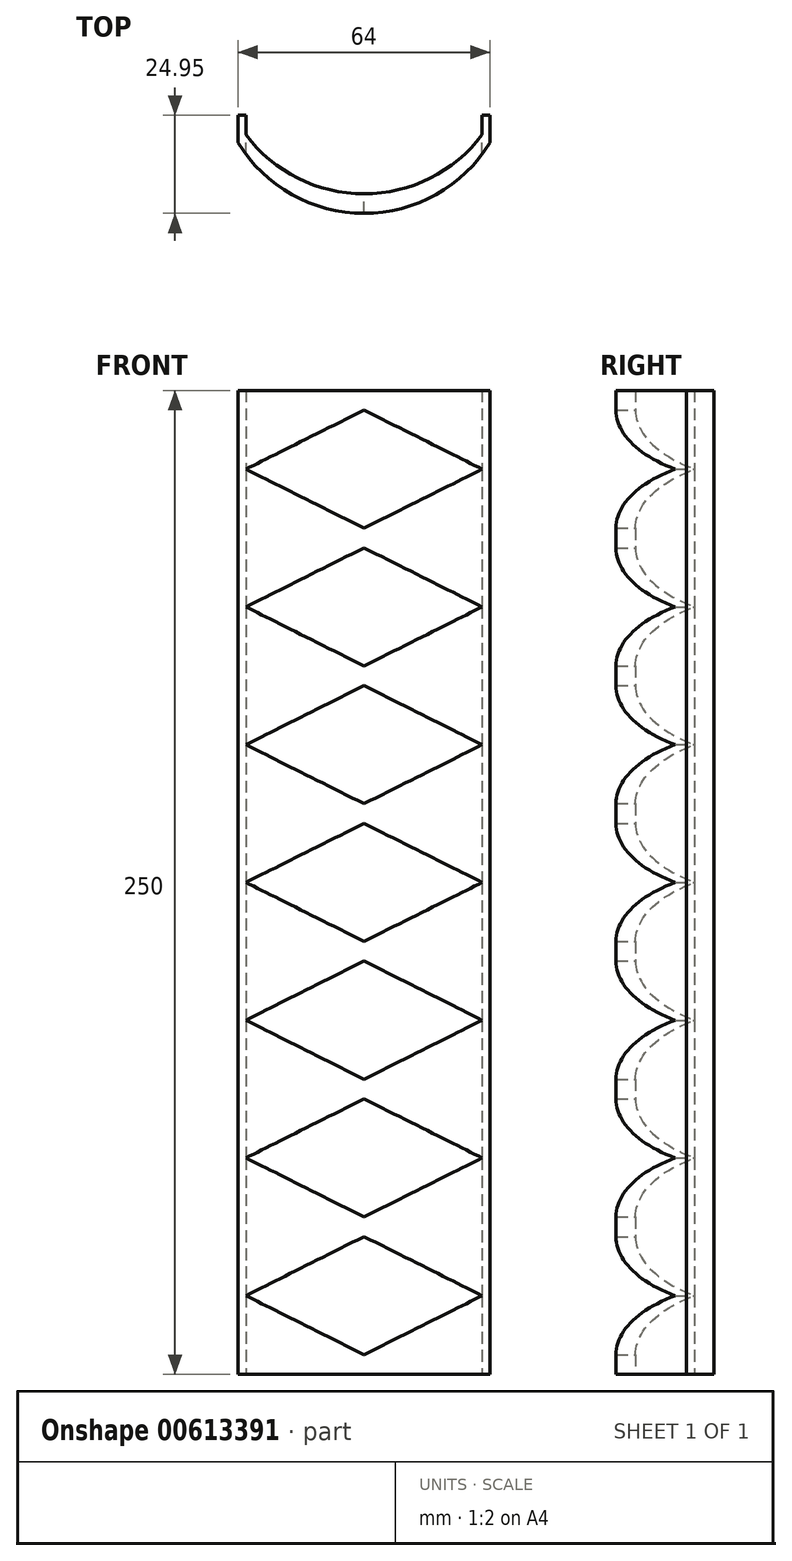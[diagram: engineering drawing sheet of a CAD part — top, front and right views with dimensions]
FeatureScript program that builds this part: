
annotation { "Feature Type Name" : "Feature", "Feature Type Description" : "" }
export const myFeature = defineFeature(function(context is Context, id is Id, definition is map)
    precondition{}
    {
        {
            var Q0;
            Q0=qCreatedBy(makeId("Top.planeOp"),FACE);
            var sketch = newSketch(context, id + "F0", { "sketchPlane" : qUnion([Q0])});
            skCircle(sketch, "E0", {"center": v(0, 0) * mm, "radius": 37.5 * mm});
            skLineSegment(sketch, "E1", {"start": v(-32, -12.55) * mm, "end": v(32, -12.55) * mm});
            skLineSegment(sketch, "E2", {"start": v(32, -12.55) * mm, "end": v(32, -19.55) * mm});
            skLineSegment(sketch, "E3", {"start": v(-32, -12.55) * mm, "end": v(-32, -19.55) * mm});
            skLineSegment(sketch, "E4", {"start": v(0, 0) * mm, "end": v(0, -12.55) * mm});
            skSolve(sketch);
        }
        {
            var Q0;
            {var subQ0=sQuery(id+"F0.wireOp",EDGE,"E2");Q0=makeQuery(id+"F0.imprint","IMPRINT",FACE,{"disambiguationData":[TD([[makeQuery(id+"F0.imprint","IMPRINT",EDGE,{"derivedFrom":subQ0}),-1.0]])]});}
            extrude(context, id + "F1", {"entities" : qUnion([Q0]), "depth" : 250 * mm, "offsetDistance" : 25 * mm});
        }
        {
            var Q0;
            Q0=makeQuery(id+"F1.opExtrude","CAP_FACE",FACE,{"disambiguationData":[OSD([sQuery(id+"F0.wireOp",EDGE,"E0"),sQuery(id+"F0.wireOp",EDGE,"E1"),sQuery(id+"F0.wireOp",EDGE,"E2"),sQuery(id+"F0.wireOp",EDGE,"E3")])],"isStart":true});
            var sketch = newSketch(context, id + "F2", { "sketchPlane" : qUnion([Q0])});
            skLineSegment(sketch, "E5", {"start": v(30, 12.55) * mm, "end": v(30, 17.55) * mm});
            skLineSegment(sketch, "E6", {"start": v(-30, 12.55) * mm, "end": v(-30, 17.55) * mm});
            skLineSegment(sketch, "E7", {"start": v(30, 12.55) * mm, "end": v(-30, 12.55) * mm});
            skCircle(sketch, "E8", {"center": v(0, -4.95) * mm, "radius": 37.5 * mm});
            skSolve(sketch);
        }
        {
            var Q0;
            {var subQ0=sQuery(id+"F2.wireOp",EDGE,"E5");Q0=makeQuery(id+"F2.imprint","IMPRINT",FACE,{"disambiguationData":[TD([[makeQuery(id+"F2.imprint","IMPRINT",EDGE,{"derivedFrom":subQ0}),1.0]])]});}
            extrude(context, id + "F3", {"entities" : qUnion([Q0]), "operationType" : NewBodyOperationType.REMOVE, "oppositeDirection" : true, "depth" : 250 * mm, "offsetDistance" : 25 * mm});
        }
        {
            var Q0;
            Q0=qCreatedBy(makeId("Front.planeOp"),FACE);
            var sketch = newSketch(context, id + "F4", { "sketchPlane" : qUnion([Q0])});
            skLineSegment(sketch, "E9", {"start": v(0, 5) * mm, "end": v(30, 20) * mm});
            skLineSegment(sketch, "E10", {"start": v(30, 20) * mm, "end": v(0, 35) * mm});
            skLineSegment(sketch, "E11", {"start": v(0, 35) * mm, "end": v(-30, 20) * mm});
            skLineSegment(sketch, "E12", {"start": v(-30, 20) * mm, "end": v(0, 5) * mm});
            skLineSegment(sketch, "E13", {"start": v(0, 40) * mm, "end": v(30, 55) * mm});
            skLineSegment(sketch, "E14", {"start": v(30, 55) * mm, "end": v(0, 70) * mm});
            skLineSegment(sketch, "E15", {"start": v(0, 70) * mm, "end": v(-30, 55) * mm});
            skLineSegment(sketch, "E16", {"start": v(-30, 55) * mm, "end": v(0, 40) * mm});
            skLineSegment(sketch, "E17", {"start": v(0, 75) * mm, "end": v(30, 90) * mm});
            skLineSegment(sketch, "E18", {"start": v(30, 90) * mm, "end": v(0, 105) * mm});
            skLineSegment(sketch, "E19", {"start": v(0, 105) * mm, "end": v(-30, 90) * mm});
            skLineSegment(sketch, "E20", {"start": v(-30, 90) * mm, "end": v(0, 75) * mm});
            skLineSegment(sketch, "E21", {"start": v(0, 110) * mm, "end": v(30, 125) * mm});
            skLineSegment(sketch, "E22", {"start": v(30, 125) * mm, "end": v(0, 140) * mm});
            skLineSegment(sketch, "E23", {"start": v(0, 140) * mm, "end": v(-30, 125) * mm});
            skLineSegment(sketch, "E24", {"start": v(-30, 125) * mm, "end": v(0, 110) * mm});
            skLineSegment(sketch, "E25", {"start": v(0, 145) * mm, "end": v(30, 160) * mm});
            skLineSegment(sketch, "E26", {"start": v(30, 160) * mm, "end": v(0, 175) * mm});
            skLineSegment(sketch, "E27", {"start": v(0, 175) * mm, "end": v(-30, 160) * mm});
            skLineSegment(sketch, "E28", {"start": v(-30, 160) * mm, "end": v(0, 145) * mm});
            skLineSegment(sketch, "E29", {"start": v(0, 180) * mm, "end": v(30, 195) * mm});
            skLineSegment(sketch, "E30", {"start": v(30, 195) * mm, "end": v(0, 210) * mm});
            skLineSegment(sketch, "E31", {"start": v(0, 210) * mm, "end": v(-30, 195) * mm});
            skLineSegment(sketch, "E32", {"start": v(-30, 195) * mm, "end": v(0, 180) * mm});
            skLineSegment(sketch, "E33", {"start": v(0, 215) * mm, "end": v(30, 230) * mm});
            skLineSegment(sketch, "E34", {"start": v(30, 230) * mm, "end": v(0, 245) * mm});
            skLineSegment(sketch, "E35", {"start": v(0, 245) * mm, "end": v(-30, 230) * mm});
            skLineSegment(sketch, "E36", {"start": v(-30, 230) * mm, "end": v(0, 215) * mm});
            skLineSegment(sketch, "E37", {"start": v(0, 250) * mm, "end": v(30, 265) * mm});
            skLineSegment(sketch, "E38", {"start": v(30, 265) * mm, "end": v(0, 280) * mm});
            skLineSegment(sketch, "E39", {"start": v(0, 280) * mm, "end": v(-30, 265) * mm});
            skLineSegment(sketch, "E40", {"start": v(-30, 265) * mm, "end": v(0, 250) * mm});
            skLineSegment(sketch, "E41", {"start": v(30, 20) * mm, "end": v(30, 287) * mm});
            skSolve(sketch);
        }
        {
            var Q0;
            Q0=makeQuery(id+"F4.imprint","IMPRINT",FACE,{"disambiguationData":[TD([[makeQuery(id+"F4.imprint","IMPRINT",EDGE,{"derivedFrom":sQuery(id+"F4.wireOp",EDGE,"E9")}),1.0]])]});
            var Q1;
            Q1=makeQuery(id+"F4.imprint","IMPRINT",FACE,{"disambiguationData":[TD([[makeQuery(id+"F4.imprint","IMPRINT",EDGE,{"derivedFrom":sQuery(id+"F4.wireOp",EDGE,"E13")}),1.0]])]});
            var Q2;
            Q2=makeQuery(id+"F4.imprint","IMPRINT",FACE,{"disambiguationData":[TD([[makeQuery(id+"F4.imprint","IMPRINT",EDGE,{"derivedFrom":sQuery(id+"F4.wireOp",EDGE,"d8b641fc-56f7-40e6-bfc2-91b29fda232b")}),1.0]])]});
            var Q3;
            Q3=makeQuery(id+"F4.imprint","IMPRINT",FACE,{"disambiguationData":[TD([[makeQuery(id+"F4.imprint","IMPRINT",EDGE,{"derivedFrom":sQuery(id+"F4.wireOp",EDGE,"388a7aa9-ebf9-4580-9e21-c3ecad2f860f")}),1.0]])]});
            var Q4;
            Q4=makeQuery(id+"F4.imprint","IMPRINT",FACE,{"disambiguationData":[TD([[makeQuery(id+"F4.imprint","IMPRINT",EDGE,{"derivedFrom":sQuery(id+"F4.wireOp",EDGE,"6b8fcc2f-93a1-496d-8120-65e9c627c765")}),1.0]])]});
            var Q5;
            Q5=makeQuery(id+"F4.imprint","IMPRINT",FACE,{"disambiguationData":[TD([[makeQuery(id+"F4.imprint","IMPRINT",EDGE,{"derivedFrom":sQuery(id+"F4.wireOp",EDGE,"22765b01-aeac-404b-a777-f358ac3c5a3e")}),1.0]])]});
            var Q6;
            Q6=makeQuery(id+"F4.imprint","IMPRINT",FACE,{"disambiguationData":[TD([[makeQuery(id+"F4.imprint","IMPRINT",EDGE,{"derivedFrom":sQuery(id+"F4.wireOp",EDGE,"3ab3fb14-603d-418e-8634-f0ea1a64353f")}),1.0]])]});
            var Q7;
            Q7=makeQuery(id+"F4.imprint","IMPRINT",FACE,{"disambiguationData":[TD([[makeQuery(id+"F4.imprint","IMPRINT",EDGE,{"derivedFrom":sQuery(id+"F4.wireOp",EDGE,"793706e1-87ed-4c42-ba7f-a15148d218aa")}),1.0]])]});
            var Q8;
            Q8=makeQuery(id+"F4.imprint","IMPRINT",FACE,{"disambiguationData":[TD([[makeQuery(id+"F4.imprint","IMPRINT",EDGE,{"derivedFrom":sQuery(id+"F4.wireOp",EDGE,"E21")}),1.0]])]});
            var Q9;
            Q9=makeQuery(id+"F4.imprint","IMPRINT",FACE,{"disambiguationData":[TD([[makeQuery(id+"F4.imprint","IMPRINT",EDGE,{"derivedFrom":sQuery(id+"F4.wireOp",EDGE,"E25")}),1.0]])]});
            var Q10;
            Q10=makeQuery(id+"F4.imprint","IMPRINT",FACE,{"disambiguationData":[TD([[makeQuery(id+"F4.imprint","IMPRINT",EDGE,{"derivedFrom":sQuery(id+"F4.wireOp",EDGE,"E29")}),1.0]])]});
            var Q11;
            Q11=makeQuery(id+"F4.imprint","IMPRINT",FACE,{"disambiguationData":[TD([[makeQuery(id+"F4.imprint","IMPRINT",EDGE,{"derivedFrom":sQuery(id+"F4.wireOp",EDGE,"E33")}),1.0]])]});
            var Q12;
            Q12=makeQuery(id+"F4.imprint","IMPRINT",FACE,{"disambiguationData":[TD([[makeQuery(id+"F4.imprint","IMPRINT",EDGE,{"derivedFrom":sQuery(id+"F4.wireOp",EDGE,"E17")}),1.0]])]});
            extrude(context, id + "F5", {"entities" : qUnion([Q0, Q1, Q2, Q3, Q4, Q5, Q6, Q7, Q8, Q9, Q10, Q11, Q12]), "operationType" : NewBodyOperationType.REMOVE, "endBound" : BoundingType.THROUGH_ALL, "depth" : 25 * mm, "offsetDistance" : 25 * mm});
        }
    });
